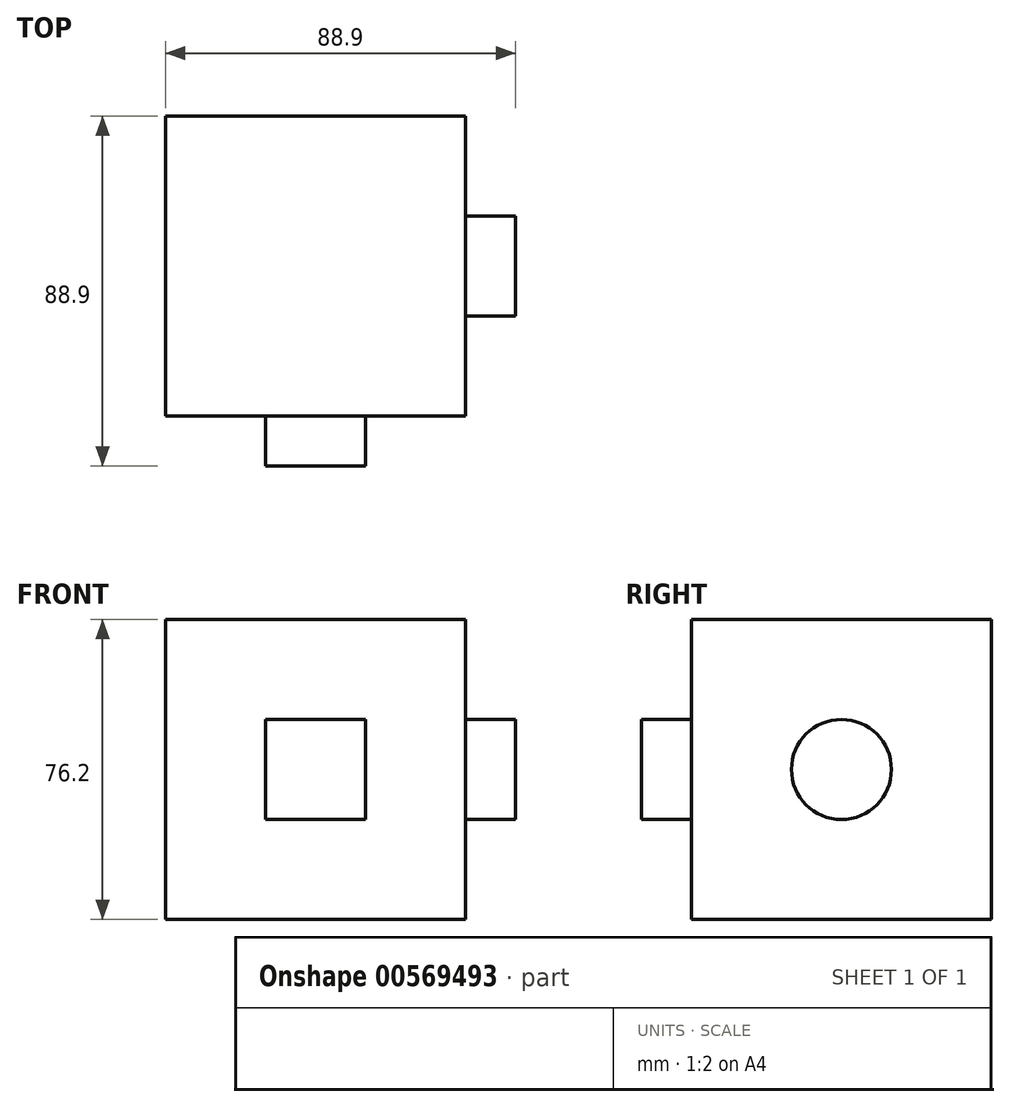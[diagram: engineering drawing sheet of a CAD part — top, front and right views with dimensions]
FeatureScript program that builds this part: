
annotation { "Feature Type Name" : "Feature", "Feature Type Description" : "" }
export const myFeature = defineFeature(function(context is Context, id is Id, definition is map)
    precondition{}
    {
        {
            var Q0;
            Q0=qCreatedBy(makeId("Front.planeOp"),FACE);
            var sketch = newSketch(context, id + "F0", { "sketchPlane" : qUnion([Q0])});
            skLineSegment(sketch, "E0.bottom", {"start": v(0, 1.72) * mm, "end": v(-76.2, 1.72) * mm});
            skLineSegment(sketch, "E0.top", {"start": v(0, 77.92) * mm, "end": v(-76.2, 77.92) * mm});
            skLineSegment(sketch, "E0.left", {"start": v(0, 1.72) * mm, "end": v(0, 77.92) * mm});
            skLineSegment(sketch, "E0.right", {"start": v(-76.2, 1.72) * mm, "end": v(-76.2, 77.92) * mm});
            skSolve(sketch);
        }
        {
            var Q0;
            Q0=makeQuery(id+"F0.imprint","IMPRINT",FACE,{"disambiguationData":[TD([[makeQuery(id+"F0.imprint","IMPRINT",EDGE,{"derivedFrom":sQuery(id+"F0.wireOp",EDGE,"E0.bottom")}),-1.0]])]});
            extrude(context, id + "F1", {"entities" : qUnion([Q0]), "depth" : 76.2 * mm, "offsetDistance" : 25.4 * mm});
        }
        {
            var Q0;
            Q0=makeQuery(id+"F1.opExtrude","CAP_FACE",FACE,{"disambiguationData":[OSD([sQuery(id+"F0.wireOp",EDGE,"E0.bottom"),sQuery(id+"F0.wireOp",EDGE,"E0.top"),sQuery(id+"F0.wireOp",EDGE,"E0.left"),sQuery(id+"F0.wireOp",EDGE,"E0.right")])],"isStart":false});
            var sketch = newSketch(context, id + "F2", { "sketchPlane" : qUnion([Q0])});
            skLineSegment(sketch, "E1.bottom", {"start": v(-50.8, 52.52) * mm, "end": v(-25.4, 52.52) * mm});
            skLineSegment(sketch, "E1.top", {"start": v(-50.8, 27.12) * mm, "end": v(-25.4, 27.12) * mm});
            skLineSegment(sketch, "E1.left", {"start": v(-50.8, 52.52) * mm, "end": v(-50.8, 27.12) * mm});
            skLineSegment(sketch, "E1.right", {"start": v(-25.4, 52.52) * mm, "end": v(-25.4, 27.12) * mm});
            skSolve(sketch);
        }
        {
            var Q0;
            Q0=makeQuery(id+"F2.imprint","IMPRINT",FACE,{"disambiguationData":[TD([[makeQuery(id+"F2.imprint","IMPRINT",EDGE,{"derivedFrom":sQuery(id+"F2.wireOp",EDGE,"E1.bottom")}),-1.0]])]});
            extrude(context, id + "F3", {"entities" : qUnion([Q0]), "operationType" : NewBodyOperationType.ADD, "depth" : 12.7 * mm, "offsetDistance" : 25.4 * mm});
        }
        {
            var Q0;
            Q0=makeQuery(id+"F1.opExtrude","SWEPT_FACE",FACE,{"disambiguationData":[OSD([sQuery(id+"F0.wireOp",EDGE,"E0.left")])]});
            var sketch = newSketch(context, id + "F4", { "sketchPlane" : qUnion([Q0])});
            skCircle(sketch, "E2", {"center": v(-38.1, 39.82) * mm, "radius": 12.7 * mm});
            skSolve(sketch);
        }
        {
            var Q0;
            Q0=makeQuery(id+"F4.imprint","IMPRINT",FACE,{"disambiguationData":[TD([[makeQuery(id+"F4.imprint","IMPRINT",EDGE,{"derivedFrom":sQuery(id+"F4.wireOp",EDGE,"E2")}),1.0]])]});
            extrude(context, id + "F5", {"entities" : qUnion([Q0]), "operationType" : NewBodyOperationType.ADD, "depth" : 12.7 * mm, "offsetDistance" : 25.4 * mm});
        }
    });
